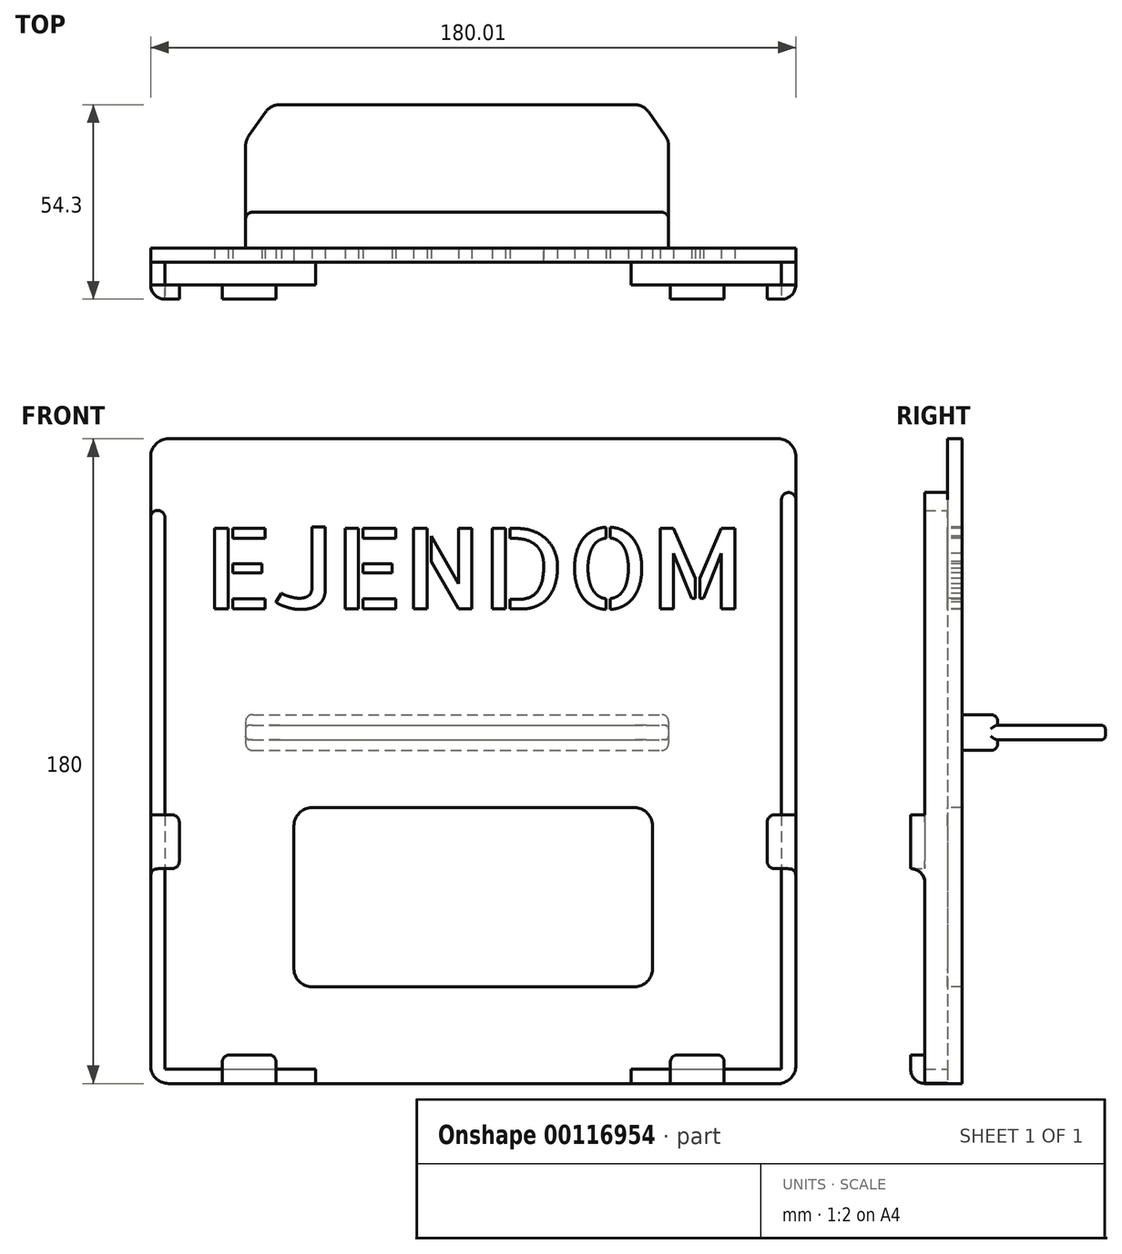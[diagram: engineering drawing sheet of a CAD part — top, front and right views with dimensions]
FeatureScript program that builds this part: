
annotation { "Feature Type Name" : "Feature", "Feature Type Description" : "" }
export const myFeature = defineFeature(function(context is Context, id is Id, definition is map)
    precondition{}
    {
        {
            var Q0;
            Q0=qCreatedBy(makeId("Top.planeOp"),FACE);
            var sketch = newSketch(context, id + "F0", { "sketchPlane" : qUnion([Q0])});
            skLineSegment(sketch, "E0.bottom", {"start": v(-29.35, 12.82) * mm, "end": v(69.44, 12.82) * mm});
            skLineSegment(sketch, "E0.top", {"start": v(-38.96, -17.18) * mm, "end": v(79.04, -17.18) * mm});
            skLineSegment(sketch, "E0.left", {"start": v(-38.96, 1.25) * mm, "end": v(-38.96, -17.18) * mm});
            skLineSegment(sketch, "E0.right", {"start": v(79.04, 1.25) * mm, "end": v(79.04, -17.18) * mm});
            skLineSegment(sketch, "E1", {"start": v(-38.05, 4.11) * mm, "end": v(-33.45, 10.7) * mm});
            skLineSegment(sketch, "E2", {"start": v(73.54, 10.7) * mm, "end": v(78.14, 4.11) * mm});
            skPoint(sketch, "E3.orphan", {"position": v(-38.96, 12.82) * mm});
            skPoint(sketch, "E4.orphan", {"position": v(79.04, 12.82) * mm});
            skPoint(sketch, "E5.visualSharp", {"position": v(-38.96, 2.82) * mm});
            skArc(sketch, "E5.filletArc", {"start": v(-38.05, 4.11) * mm, "mid": v(-38.73, 2.75) * mm, "end": v(-38.96, 1.25) * mm});
            skPoint(sketch, "E6.visualSharp", {"position": v(-31.96, 12.82) * mm});
            skArc(sketch, "E6.filletArc", {"start": v(-29.35, 12.82) * mm, "mid": v(-31.66, 12.26) * mm, "end": v(-33.45, 10.7) * mm});
            skPoint(sketch, "E7.visualSharp", {"position": v(72.04, 12.82) * mm});
            skArc(sketch, "E7.filletArc", {"start": v(73.54, 10.7) * mm, "mid": v(71.75, 12.26) * mm, "end": v(69.44, 12.82) * mm});
            skPoint(sketch, "E8.visualSharp", {"position": v(79.04, 2.82) * mm});
            skArc(sketch, "E8.filletArc", {"start": v(79.04, 1.25) * mm, "mid": v(78.81, 2.75) * mm, "end": v(78.14, 4.11) * mm});
            skSolve(sketch);
        }
        {
            var Q0;
            Q0 = qSketchRegion(id + "F0", true);
            extrude(context, id + "F1", {"entities" : qUnion([Q0]), "depth" : 4 * mm});
        }
        {
            var Q0;
            Q0=makeQuery(id+"F1.opExtrude","CAP_EDGE",EDGE,{"disambiguationData":[OSD([sQuery(id+"F0.wireOp",EDGE,"E0.left")])],"isStart":false});
            var Q1;
            Q1=makeQuery(id+"F1.opExtrude","CAP_EDGE",EDGE,{"disambiguationData":[OSD([sQuery(id+"F0.wireOp",EDGE,"E0.right")])],"isStart":true});
            fillet(context, id + "F2", {"entities" : qUnion([Q0, Q1]), "radius" : 1 * mm, "tangentPropagation" : true, "allowEdgeOverflow" : false});
        }
        {
            var Q0;
            Q0=makeQuery(id+"F1.opExtrude","SWEPT_FACE",FACE,{"disambiguationData":[OSD([sQuery(id+"F0.wireOp",EDGE,"E0.top")])]});
            var sketch = newSketch(context, id + "F3", { "sketchPlane" : qUnion([Q0])});
            skLineSegment(sketch, "E9.bottom", {"start": v(-38.96, 7) * mm, "end": v(79.04, 7) * mm});
            skLineSegment(sketch, "E9.top", {"start": v(-38.96, -3) * mm, "end": v(79.04, -3) * mm});
            skLineSegment(sketch, "E9.left", {"start": v(-38.96, 7) * mm, "end": v(-38.96, -3) * mm});
            skLineSegment(sketch, "E9.right", {"start": v(79.04, 7) * mm, "end": v(79.04, -3) * mm});
            skSolve(sketch);
        }
        {
            var Q0;
            Q0 = qSketchRegion(id + "F3", true);
            extrude(context, id + "F4", {"entities" : qUnion([Q0]), "operationType" : NewBodyOperationType.ADD, "depth" : 10 * mm});
        }
        {
            var Q0;
            Q0=makeQuery(id+"F4.opExtrude","SWEPT_EDGE",EDGE,{"disambiguationData":[OSD([sQuery(id+"F3.wireOp",EDGE,"E9.bottom"),sQuery(id+"F3.wireOp",EDGE,"E9.left")])]});
            var Q1;
            Q1=makeQuery(id+"F4.opExtrude","CAP_EDGE",EDGE,{"disambiguationData":[OSD([sQuery(id+"F3.wireOp",EDGE,"E9.bottom")])],"isStart":true});
            var Q2;
            Q2=makeQuery(id+"F4.opExtrude","SWEPT_EDGE",EDGE,{"disambiguationData":[OSD([sQuery(id+"F3.wireOp",EDGE,"E9.bottom"),sQuery(id+"F3.wireOp",EDGE,"E9.right")])]});
            var Q3;
            Q3=makeQuery(id+"F4.opExtrude","SWEPT_EDGE",EDGE,{"disambiguationData":[OSD([sQuery(id+"F3.wireOp",EDGE,"E9.top"),sQuery(id+"F3.wireOp",EDGE,"E9.left")])]});
            var Q4;
            Q4=makeQuery(id+"F4.opExtrude","CAP_EDGE",EDGE,{"disambiguationData":[OSD([sQuery(id+"F3.wireOp",EDGE,"E9.top")])],"isStart":true});
            var Q5;
            Q5=makeQuery(id+"F4.opExtrude","SWEPT_EDGE",EDGE,{"disambiguationData":[OSD([sQuery(id+"F3.wireOp",EDGE,"E9.top"),sQuery(id+"F3.wireOp",EDGE,"E9.right")])]});
            var Q6;
            {var subQ0=sQuery(id+"F3.wireOp",EDGE,"E9.left");var subQ1=sQuery(id+"F3.wireOp",EDGE,"E9.bottom");Q6=makeQuery(id+"F4.boolean.opBoolean","SPLIT",EDGE,{"disambiguationData":[TD([makeQuery(id+"F4.opExtrude","SWEPT_FACE",FACE,{"disambiguationData":[OSD([subQ1])]})])],"derivedFrom":makeQuery(id+"F4.opExtrude","CAP_EDGE",EDGE,{"disambiguationData":[OSD([subQ0])],"isStart":true})});}
            var Q7;
            {var subQ0=sQuery(id+"F3.wireOp",EDGE,"E9.top");var subQ1=sQuery(id+"F3.wireOp",EDGE,"E9.left");Q7=makeQuery(id+"F4.boolean.opBoolean","SPLIT",EDGE,{"disambiguationData":[TD([makeQuery(id+"F4.opExtrude","SWEPT_FACE",FACE,{"disambiguationData":[OSD([subQ0])]})])],"derivedFrom":makeQuery(id+"F4.opExtrude","CAP_EDGE",EDGE,{"disambiguationData":[OSD([subQ1])],"isStart":true})});}
            var Q8;
            {var subQ0=sQuery(id+"F3.wireOp",EDGE,"E9.right");var subQ1=sQuery(id+"F3.wireOp",EDGE,"E9.bottom");Q8=makeQuery(id+"F4.boolean.opBoolean","SPLIT",EDGE,{"disambiguationData":[TD([makeQuery(id+"F4.opExtrude","SWEPT_FACE",FACE,{"disambiguationData":[OSD([subQ1])]})])],"derivedFrom":makeQuery(id+"F4.opExtrude","CAP_EDGE",EDGE,{"disambiguationData":[OSD([subQ0])],"isStart":true})});}
            var Q9;
            {var subQ0=sQuery(id+"F3.wireOp",EDGE,"E9.top");var subQ1=sQuery(id+"F3.wireOp",EDGE,"E9.right");Q9=makeQuery(id+"F4.boolean.opBoolean","SPLIT",EDGE,{"disambiguationData":[TD([makeQuery(id+"F4.opExtrude","SWEPT_FACE",FACE,{"disambiguationData":[OSD([subQ0])]})])],"derivedFrom":makeQuery(id+"F4.opExtrude","CAP_EDGE",EDGE,{"disambiguationData":[OSD([subQ1])],"isStart":true})});}
            fillet(context, id + "F5", {"entities" : qUnion([Q0, Q1, Q2, Q3, Q4, Q5, Q6, Q7, Q8, Q9]), "radius" : 2 * mm, "tangentPropagation" : true, "allowEdgeOverflow" : false});
        }
        {
            var Q0;
            Q0=makeQuery(id+"F4.opExtrude","CAP_FACE",FACE,{"disambiguationData":[OSD([sQuery(id+"F3.wireOp",EDGE,"E9.bottom"),sQuery(id+"F3.wireOp",EDGE,"E9.top"),sQuery(id+"F3.wireOp",EDGE,"E9.left"),sQuery(id+"F3.wireOp",EDGE,"E9.right")])],"isStart":false});
            var sketch = newSketch(context, id + "F6", { "sketchPlane" : qUnion([Q0])});
            skLineSegment(sketch, "E10.bottom", {"start": v(-60.46, 84) * mm, "end": v(109.54, 84) * mm});
            skLineSegment(sketch, "E10.top", {"start": v(-60.46, -96) * mm, "end": v(-51.46, -96) * mm});
            skLineSegment(sketch, "E10.left", {"start": v(-65.46, 79) * mm, "end": v(-65.46, 50) * mm});
            skLineSegment(sketch, "E10.right", {"start": v(114.54, 79) * mm, "end": v(114.54, 50) * mm});
            skPoint(sketch, "E11.visualSharp", {"position": v(-65.46, 84) * mm});
            skArc(sketch, "E11.filletArc", {"start": v(-60.46, 84) * mm, "mid": v(-64, 82.54) * mm, "end": v(-65.46, 79) * mm});
            skPoint(sketch, "E12.visualSharp", {"position": v(114.54, 84) * mm});
            skArc(sketch, "E12.filletArc", {"start": v(114.54, 79) * mm, "mid": v(113.08, 82.54) * mm, "end": v(109.54, 84) * mm});
            skPoint(sketch, "E13.visualSharp", {"position": v(114.54, -96) * mm});
            skArc(sketch, "E13.filletArc", {"start": v(109.54, -96) * mm, "mid": v(113.08, -94.54) * mm, "end": v(114.54, -91) * mm});
            skArc(sketch, "E14.filletArc", {"start": v(-65.46, -91) * mm, "mid": v(-64, -94.54) * mm, "end": v(-60.46, -96) * mm});
            skLineSegment(sketch, "E15.left", {"start": v(114.54, 44) * mm, "end": v(114.54, 9) * mm});
            skLineSegment(sketch, "E16.left", {"start": v(-65.46, 44) * mm, "end": v(-65.46, 9) * mm});
            skLineSegment(sketch, "E17", {"start": v(-10.46, -96) * mm, "end": v(50.54, -96) * mm});
            skLineSegment(sketch, "E18", {"start": v(91.54, -96) * mm, "end": v(109.54, -96) * mm});
            skPoint(sketch, "E19.newPointB", {"position": v(-65.46, 44) * mm});
            skPoint(sketch, "E20.newPointB", {"position": v(105.54, 44) * mm});
            skLineSegment(sketch, "E21", {"start": v(-65.46, 9) * mm, "end": v(-65.46, -31) * mm});
            skLineSegment(sketch, "E22", {"start": v(-65.46, -72) * mm, "end": v(-65.46, -91) * mm});
            skLineSegment(sketch, "E23", {"start": v(114.54, 9) * mm, "end": v(114.54, -31) * mm});
            skLineSegment(sketch, "E24", {"start": v(114.54, -72) * mm, "end": v(114.54, -91) * mm});
            skPoint(sketch, "E25.visualSharp", {"position": v(114.54, -66) * mm});
            skLineSegment(sketch, "E26", {"start": v(-65.46, 79) * mm, "end": v(-65.46, -31) * mm});
            skLineSegment(sketch, "E27", {"start": v(114.54, 50) * mm, "end": v(114.54, -31) * mm});
            skLineSegment(sketch, "E28", {"start": v(-65.46, -31) * mm, "end": v(-65.46, -72) * mm});
            skLineSegment(sketch, "E29", {"start": v(-51.46, -96) * mm, "end": v(-10.46, -96) * mm});
            skLineSegment(sketch, "E30", {"start": v(50.54, -96) * mm, "end": v(91.54, -96) * mm});
            skLineSegment(sketch, "E31", {"start": v(114.54, -72) * mm, "end": v(114.54, -31) * mm});
            skSolve(sketch);
        }
        {
            var Q0;
            Q0 = qSketchRegion(id + "F6", true);
            extrude(context, id + "F7", {"entities" : qUnion([Q0]), "operationType" : NewBodyOperationType.ADD, "depth" : 4 * mm});
        }
        {
            var Q0;
            Q0=makeQuery(id+"F7.opExtrude","CAP_FACE",FACE,{"disambiguationData":[OSD([sQuery(id+"F6.wireOp",EDGE,"E10.bottom"),sQuery(id+"F6.wireOp",EDGE,"E10.top"),sQuery(id+"F6.wireOp",EDGE,"E10.left"),sQuery(id+"F6.wireOp",EDGE,"E10.right")])],"isStart":false});
            var sketch = newSketch(context, id + "F8", { "sketchPlane" : qUnion([Q0])});
            skLineSegment(sketch, "E32.bottom", {"start": v(-20.46, -19) * mm, "end": v(69.54, -19) * mm});
            skLineSegment(sketch, "E32.top", {"start": v(-20.46, -69) * mm, "end": v(69.54, -69) * mm});
            skLineSegment(sketch, "E32.left", {"start": v(-25.46, -24) * mm, "end": v(-25.46, -64) * mm});
            skLineSegment(sketch, "E32.right", {"start": v(74.54, -24) * mm, "end": v(74.54, -64) * mm});
            skPoint(sketch, "E33.visualSharp", {"position": v(-25.46, -19) * mm});
            skArc(sketch, "E33.filletArc", {"start": v(-20.46, -19) * mm, "mid": v(-24, -20.46) * mm, "end": v(-25.46, -24) * mm});
            skPoint(sketch, "E34.visualSharp", {"position": v(74.54, -19) * mm});
            skArc(sketch, "E34.filletArc", {"start": v(74.54, -24) * mm, "mid": v(73.08, -20.46) * mm, "end": v(69.54, -19) * mm});
            skPoint(sketch, "E35.visualSharp", {"position": v(74.54, -69) * mm});
            skArc(sketch, "E35.filletArc", {"start": v(69.54, -69) * mm, "mid": v(73.08, -67.54) * mm, "end": v(74.54, -64) * mm});
            skPoint(sketch, "E36.visualSharp", {"position": v(-25.46, -69) * mm});
            skArc(sketch, "E36.filletArc", {"start": v(-25.46, -64) * mm, "mid": v(-24, -67.54) * mm, "end": v(-20.46, -69) * mm});
            skLineSegment(sketch, "E37", {"start": v(24.54, 111.58) * mm, "end": v(24.54, -125.34) * mm, "construction": true});
            skSolve(sketch);
        }
        {
            var Q0;
            Q0 = qSketchRegion(id + "F8", true);
            extrude(context, id + "F9", {"entities" : qUnion([Q0]), "operationType" : NewBodyOperationType.REMOVE, "oppositeDirection" : true, "depth" : 25 * mm});
        }
        {
            var Q0;
            Q0=makeQuery(id+"F7.opExtrude","CAP_FACE",FACE,{"disambiguationData":[OSD([sQuery(id+"F6.wireOp",EDGE,"E10.bottom"),sQuery(id+"F6.wireOp",EDGE,"E10.top"),sQuery(id+"F6.wireOp",EDGE,"E10.left"),sQuery(id+"F6.wireOp",EDGE,"E10.right"),sQuery(id+"F6.wireOp",EDGE,"E11.filletArc"),sQuery(id+"F6.wireOp",EDGE,"E12.filletArc"),sQuery(id+"F6.wireOp",EDGE,"E13.filletArc"),sQuery(id+"F6.wireOp",EDGE,"E14.filletArc")])],"isStart":false});
            var sketch = newSketch(context, id + "F10", { "sketchPlane" : qUnion([Q0])});
            skText(sketch, "E38", { "text": "EJENDOM", "fontName": "AllertaStencil-Regular.ttf"});
            const initialGuessF10  = {"E38": [-0.05046, 0.0365, 1, 0, 0.0225]};
            skSetInitialGuess(sketch, initialGuessF10);
            skSolve(sketch);
        }
        {
            var Q0;
            Q0 = qSketchRegion(id + "F10", true);
            extrude(context, id + "F11", {"entities" : qUnion([Q0]), "operationType" : NewBodyOperationType.REMOVE, "oppositeDirection" : true, "depth" : 25 * mm});
        }
        {
            var Q0;
            Q0=makeQuery(id+"F7.opExtrude","CAP_FACE",FACE,{"disambiguationData":[OSD([sQuery(id+"F6.wireOp",EDGE,"E10.bottom"),sQuery(id+"F6.wireOp",EDGE,"E10.top"),sQuery(id+"F6.wireOp",EDGE,"E10.right"),sQuery(id+"F6.wireOp",EDGE,"E11.filletArc"),sQuery(id+"F6.wireOp",EDGE,"E12.filletArc"),sQuery(id+"F6.wireOp",EDGE,"E13.filletArc"),sQuery(id+"F6.wireOp",EDGE,"E14.filletArc"),sQuery(id+"F6.wireOp",EDGE,"E17"),sQuery(id+"F6.wireOp",EDGE,"E18"),sQuery(id+"F6.wireOp",EDGE,"E22"),sQuery(id+"F6.wireOp",EDGE,"E24"),sQuery(id+"F6.wireOp",EDGE,"E26"),sQuery(id+"F6.wireOp",EDGE,"E27"),sQuery(id+"F6.wireOp",EDGE,"E28"),sQuery(id+"F6.wireOp",EDGE,"E29"),sQuery(id+"F6.wireOp",EDGE,"E30"),sQuery(id+"F6.wireOp",EDGE,"E31")])],"isStart":false});
            var sketch = newSketch(context, id + "F12", { "sketchPlane" : qUnion([Q0])});
            skLineSegment(sketch, "E39.bottom", {"start": v(-63.46, 64) * mm, "end": v(-63.46, 64) * mm});
            skLineSegment(sketch, "E39.left", {"start": v(-65.46, 62) * mm, "end": v(-65.46, -92) * mm});
            skLineSegment(sketch, "E39.right", {"start": v(-61.46, 62) * mm, "end": v(-61.46, -96) * mm});
            skLineSegment(sketch, "E40.bottom", {"start": v(-60.46, -96) * mm, "end": v(-19.46, -96) * mm});
            skLineSegment(sketch, "E40.top", {"start": v(-65.46, -92) * mm, "end": v(-19.46, -92) * mm});
            skLineSegment(sketch, "E40.left", {"start": v(-65.46, -92) * mm, "end": v(-65.46, -91) * mm});
            skLineSegment(sketch, "E41.bottom", {"start": v(112.54, 69) * mm, "end": v(112.54, 69) * mm});
            skLineSegment(sketch, "E41.top", {"start": v(110.54, -96) * mm, "end": v(109.54, -96) * mm});
            skLineSegment(sketch, "E41.left", {"start": v(114.54, 67) * mm, "end": v(114.54, -91) * mm});
            skLineSegment(sketch, "E41.right", {"start": v(110.54, 67) * mm, "end": v(110.54, -96) * mm});
            skPoint(sketch, "E42.visualSharp", {"position": v(-65.46, -96) * mm});
            skArc(sketch, "E42.filletArc", {"start": v(-65.46, -91) * mm, "mid": v(-64, -94.54) * mm, "end": v(-60.46, -96) * mm});
            skPoint(sketch, "E43.visualSharp", {"position": v(114.54, -96) * mm});
            skArc(sketch, "E43.filletArc", {"start": v(109.54, -96) * mm, "mid": v(113.08, -94.54) * mm, "end": v(114.54, -91) * mm});
            skPoint(sketch, "E44.visualSharp", {"position": v(-65.46, 64) * mm});
            skArc(sketch, "E44.filletArc", {"start": v(-63.46, 64) * mm, "mid": v(-64.87, 63.41) * mm, "end": v(-65.46, 62) * mm});
            skPoint(sketch, "E45.visualSharp", {"position": v(-61.46, 64) * mm});
            skArc(sketch, "E45.filletArc", {"start": v(-61.46, 62) * mm, "mid": v(-62.04, 63.41) * mm, "end": v(-63.46, 64) * mm});
            skPoint(sketch, "E46.visualSharp", {"position": v(110.54, 69) * mm});
            skArc(sketch, "E46.filletArc", {"start": v(112.54, 69) * mm, "mid": v(111.13, 68.41) * mm, "end": v(110.54, 67) * mm});
            skPoint(sketch, "E47.visualSharp", {"position": v(114.54, 69) * mm});
            skArc(sketch, "E47.filletArc", {"start": v(114.54, 67) * mm, "mid": v(113.96, 68.41) * mm, "end": v(112.54, 69) * mm});
            skLineSegment(sketch, "E48", {"start": v(-19.46, -92) * mm, "end": v(-19.46, -96) * mm});
            skLineSegment(sketch, "E49", {"start": v(68.54, -92) * mm, "end": v(68.54, -96) * mm});
            skLineSegment(sketch, "E50.trimOffspring", {"start": v(68.54, -92) * mm, "end": v(114.54, -92) * mm});
            skLineSegment(sketch, "E51.trimOffspring", {"start": v(68.54, -96) * mm, "end": v(110.54, -96) * mm});
            skSolve(sketch);
        }
        {
            var Q0;
            Q0 = qSketchRegion(id + "F12", true);
            extrude(context, id + "F13", {"entities" : qUnion([Q0]), "operationType" : NewBodyOperationType.ADD, "depth" : 6.3 * mm});
        }
        {
            var Q0;
            Q0=makeQuery(id+"F13.opExtrude","CAP_FACE",FACE,{"disambiguationData":[OSD([sQuery(id+"F12.wireOp",EDGE,"E39.left"),sQuery(id+"F12.wireOp",EDGE,"E39.right"),sQuery(id+"F12.wireOp",EDGE,"E40.bottom"),sQuery(id+"F12.wireOp",EDGE,"E40.top"),sQuery(id+"F12.wireOp",EDGE,"E40.left"),sQuery(id+"F12.wireOp",EDGE,"E42.filletArc"),sQuery(id+"F12.wireOp",EDGE,"E44.filletArc"),sQuery(id+"F12.wireOp",EDGE,"E45.filletArc"),sQuery(id+"F12.wireOp",EDGE,"E48")])],"isStart":false});
            var sketch = newSketch(context, id + "F14", { "sketchPlane" : qUnion([Q0])});
            skLineSegment(sketch, "E52.bottom", {"start": v(-65.46, -21) * mm, "end": v(-59.46, -21) * mm});
            skLineSegment(sketch, "E52.top", {"start": v(-65.46, -36) * mm, "end": v(-59.46, -36) * mm});
            skLineSegment(sketch, "E52.left", {"start": v(-65.46, -21) * mm, "end": v(-65.46, -36) * mm});
            skLineSegment(sketch, "E52.right", {"start": v(-57.46, -23) * mm, "end": v(-57.46, -34) * mm});
            skLineSegment(sketch, "E53.bottom", {"start": v(108.54, -21) * mm, "end": v(114.54, -21) * mm});
            skLineSegment(sketch, "E53.top", {"start": v(108.54, -36) * mm, "end": v(114.54, -36) * mm});
            skLineSegment(sketch, "E53.left", {"start": v(106.54, -23) * mm, "end": v(106.54, -34) * mm});
            skLineSegment(sketch, "E53.right", {"start": v(114.54, -21) * mm, "end": v(114.54, -36) * mm});
            skLineSegment(sketch, "E54.bottom", {"start": v(-45.46, -96) * mm, "end": v(-30.46, -96) * mm});
            skLineSegment(sketch, "E54.top", {"start": v(-43.46, -88) * mm, "end": v(-32.46, -88) * mm});
            skLineSegment(sketch, "E54.left", {"start": v(-45.46, -96) * mm, "end": v(-45.46, -90) * mm});
            skLineSegment(sketch, "E54.right", {"start": v(-30.46, -96) * mm, "end": v(-30.46, -90) * mm});
            skLineSegment(sketch, "E55.bottom", {"start": v(81.54, -88) * mm, "end": v(92.54, -88) * mm});
            skLineSegment(sketch, "E55.top", {"start": v(79.54, -96) * mm, "end": v(94.54, -96) * mm});
            skLineSegment(sketch, "E55.left", {"start": v(79.54, -90) * mm, "end": v(79.54, -96) * mm});
            skLineSegment(sketch, "E55.right", {"start": v(94.54, -90) * mm, "end": v(94.54, -96) * mm});
            skPoint(sketch, "E56.visualSharp", {"position": v(-45.46, -88) * mm});
            skArc(sketch, "E56.filletArc", {"start": v(-43.46, -88) * mm, "mid": v(-44.87, -88.59) * mm, "end": v(-45.46, -90) * mm});
            skPoint(sketch, "E57.visualSharp", {"position": v(-30.46, -88) * mm});
            skArc(sketch, "E57.filletArc", {"start": v(-30.46, -90) * mm, "mid": v(-31.04, -88.59) * mm, "end": v(-32.46, -88) * mm});
            skPoint(sketch, "E58.visualSharp", {"position": v(79.54, -88) * mm});
            skArc(sketch, "E58.filletArc", {"start": v(81.54, -88) * mm, "mid": v(80.13, -88.59) * mm, "end": v(79.54, -90) * mm});
            skPoint(sketch, "E59.visualSharp", {"position": v(94.54, -88) * mm});
            skArc(sketch, "E59.filletArc", {"start": v(94.54, -90) * mm, "mid": v(93.96, -88.59) * mm, "end": v(92.54, -88) * mm});
            skPoint(sketch, "E60.visualSharp", {"position": v(106.54, -36) * mm});
            skArc(sketch, "E60.filletArc", {"start": v(106.54, -34) * mm, "mid": v(107.13, -35.41) * mm, "end": v(108.54, -36) * mm});
            skPoint(sketch, "E61.visualSharp", {"position": v(106.54, -21) * mm});
            skArc(sketch, "E61.filletArc", {"start": v(108.54, -21) * mm, "mid": v(107.13, -21.59) * mm, "end": v(106.54, -23) * mm});
            skPoint(sketch, "E62.visualSharp", {"position": v(-57.46, -36) * mm});
            skArc(sketch, "E62.filletArc", {"start": v(-59.46, -36) * mm, "mid": v(-58.04, -35.41) * mm, "end": v(-57.46, -34) * mm});
            skPoint(sketch, "E63.visualSharp", {"position": v(-57.46, -21) * mm});
            skArc(sketch, "E63.filletArc", {"start": v(-57.46, -23) * mm, "mid": v(-58.04, -21.59) * mm, "end": v(-59.46, -21) * mm});
            skSolve(sketch);
        }
        {
            var Q0;
            Q0 = qSketchRegion(id + "F14", true);
            extrude(context, id + "F15", {"entities" : qUnion([Q0]), "operationType" : NewBodyOperationType.ADD, "depth" : 4 * mm});
        }
        {
            var Q0;
            Q0=makeQuery(id+"F15.opExtrude","CAP_EDGE",EDGE,{"disambiguationData":[OSD([sQuery(id+"F14.wireOp",EDGE,"E52.left")])],"isStart":false});
            var Q1;
            Q1=makeQuery(id+"F15.opExtrude","CAP_EDGE",EDGE,{"disambiguationData":[OSD([sQuery(id+"F14.wireOp",EDGE,"E54.bottom")])],"isStart":false});
            var Q2;
            Q2=makeQuery(id+"F15.opExtrude","CAP_EDGE",EDGE,{"disambiguationData":[OSD([sQuery(id+"F14.wireOp",EDGE,"E53.right")])],"isStart":false});
            var Q3;
            Q3=makeQuery(id+"F15.opExtrude","CAP_EDGE",EDGE,{"disambiguationData":[OSD([sQuery(id+"F14.wireOp",EDGE,"E55.top")])],"isStart":false});
            fillet(context, id + "F16", {"entities" : qUnion([Q0, Q1, Q2, Q3]), "radius" : 4 * mm, "tangentPropagation" : true, "allowEdgeOverflow" : false});
        }
        {
            var Q0;
            {var subQ0=sQuery(id+"F14.wireOp",EDGE,"E52.top");Q0=makeQuery(id+"F15.boolean.opBoolean","SPLIT",EDGE,{"disambiguationData":[topologyDisambiguationEdgeConnected([makeQuery(id+"F13.opExtrude","CAP_FACE",FACE,{"disambiguationData":[OSD([sQuery(id+"F12.wireOp",EDGE,"E39.left"),sQuery(id+"F12.wireOp",EDGE,"E39.right"),sQuery(id+"F12.wireOp",EDGE,"E40.bottom"),sQuery(id+"F12.wireOp",EDGE,"E40.top"),sQuery(id+"F12.wireOp",EDGE,"E40.left"),sQuery(id+"F12.wireOp",EDGE,"E42.filletArc"),sQuery(id+"F12.wireOp",EDGE,"E44.filletArc"),sQuery(id+"F12.wireOp",EDGE,"E45.filletArc"),sQuery(id+"F12.wireOp",EDGE,"E48")])],"isStart":false})])],"derivedFrom":makeQuery(id+"F15.opExtrude","CAP_EDGE",EDGE,{"disambiguationData":[OSD([subQ0])],"isStart":true})});}
            var Q1;
            {var subQ0=sQuery(id+"F14.wireOp",EDGE,"E53.top");Q1=makeQuery(id+"F15.boolean.opBoolean","SPLIT",EDGE,{"disambiguationData":[topologyDisambiguationEdgeConnected([makeQuery(id+"F13.opExtrude","CAP_FACE",FACE,{"disambiguationData":[OSD([sQuery(id+"F12.wireOp",EDGE,"E41.left"),sQuery(id+"F12.wireOp",EDGE,"E41.right"),sQuery(id+"F12.wireOp",EDGE,"E43.filletArc"),sQuery(id+"F12.wireOp",EDGE,"E46.filletArc"),sQuery(id+"F12.wireOp",EDGE,"E47.filletArc"),sQuery(id+"F12.wireOp",EDGE,"E49"),sQuery(id+"F12.wireOp",EDGE,"E50.trimOffspring"),sQuery(id+"F12.wireOp",EDGE,"E51.trimOffspring")])],"isStart":false})])],"derivedFrom":makeQuery(id+"F15.opExtrude","CAP_EDGE",EDGE,{"disambiguationData":[OSD([subQ0])],"isStart":true})});}
            fillet(context, id + "F17", {"entities" : qUnion([Q0, Q1]), "radius" : 4 * mm, "tangentPropagation" : true, "allowEdgeOverflow" : false});
        }
    });
